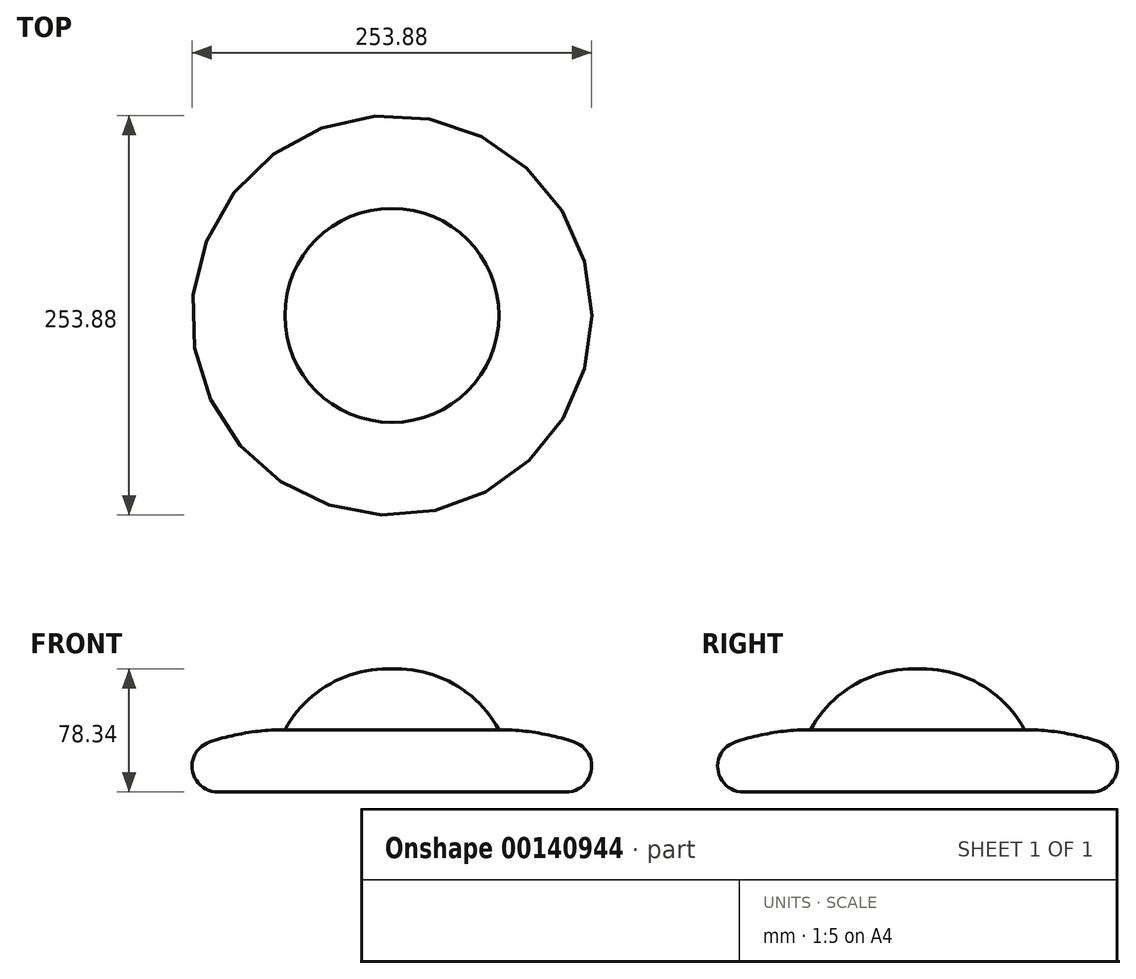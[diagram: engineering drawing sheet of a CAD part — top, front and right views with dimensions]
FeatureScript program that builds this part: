
annotation { "Feature Type Name" : "Feature", "Feature Type Description" : "" }
export const myFeature = defineFeature(function(context is Context, id is Id, definition is map)
    precondition{}
    {
        {
            var Q0;
            Q0=qCreatedBy(makeId("Top.planeOp"),FACE);
            var sketch = newSketch(context, id + "F0", { "sketchPlane" : qUnion([Q0])});
            skCircle(sketch, "E0", {"center": v(0, 0) * mm, "radius": 169.78 * mm});
            skSolve(sketch);
        }
        {
            var Q0;
            Q0=makeQuery(id+"F0.imprint","IMPRINT",FACE,{"disambiguationData":[TD([[makeQuery(id+"F0.imprint","IMPRINT",EDGE,{"derivedFrom":sQuery(id+"F0.wireOp",EDGE,"E0")}),1.0]])]});
            extrude(context, id + "F1", {"entities" : qUnion([Q0]), "depth" : 39.57 * mm});
        }
        {
            var Q0;
            Q0=makeQuery(id+"F1.opExtrude","CAP_EDGE",EDGE,{"disambiguationData":[OSD([sQuery(id+"F0.wireOp",EDGE,"E0")])],"isStart":false});
            fillet(context, id + "F2", {"entities" : qUnion([Q0]), "radius" : 150.72 * mm, "tangentPropagation" : true, "allowEdgeOverflow" : false});
        }
        {
            var Q0;
            Q0=makeQuery(id+"F1.opExtrude","CAP_FACE",FACE,{"disambiguationData":[OSD([sQuery(id+"F0.wireOp",EDGE,"E0")])],"isStart":false});
            extrude(context, id + "F3", {"entities" : qUnion([Q0]), "operationType" : NewBodyOperationType.ADD, "depth" : 38.77 * mm});
        }
        {
            var Q0;
            Q0=makeQuery(id+"F3.opExtrude","CAP_EDGE",EDGE,{"disambiguationData":[OSD([sQuery(id+"F0.wireOp",EDGE,"E0")])],"isStart":false});
            fillet(context, id + "F4", {"entities" : qUnion([Q0]), "radius" : 74.5 * mm, "tangentPropagation" : true, "allowEdgeOverflow" : false});
        }
        {
            var Q0;
            {var subQ0=sQuery(id+"F0.wireOp",EDGE,"E0");Q0=makeQuery(id+"F2.opFillet","BLEND_EDGE",EDGE,{"blendedFrom":[makeQuery(id+"F1.opExtrude","CAP_EDGE",EDGE,{"disambiguationData":[OSD([subQ0])],"isStart":false}),makeQuery(id+"F1.opExtrude","CAP_FACE",FACE,{"disambiguationData":[OSD([subQ0])],"isStart":true})],"blendedInto":[makeQuery(id+"F1.opExtrude","CAP_FACE",FACE,{"disambiguationData":[OSD([subQ0])],"isStart":true})]});}
            fillet(context, id + "F5", {"entities" : qUnion([Q0]), "radius" : 16.3 * mm, "tangentPropagation" : true, "allowEdgeOverflow" : false});
        }
    });
